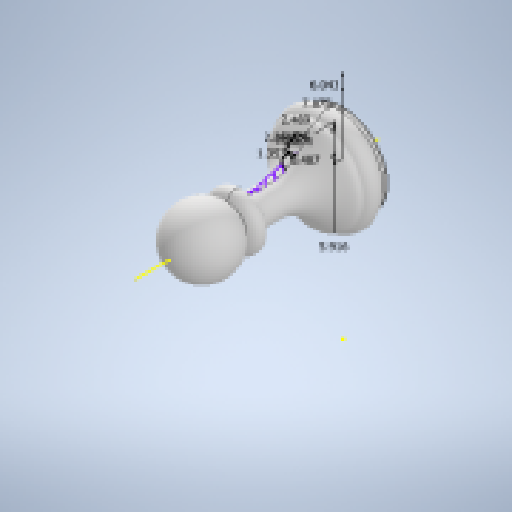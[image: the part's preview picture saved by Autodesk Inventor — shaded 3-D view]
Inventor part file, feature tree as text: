
AUTODESK INVENTOR PART (.ipt)
format: ipt  version: 2024.1 (Build 281209000, 209)  size: 1,490,432 bytes
history: native  units: mm
features: other x13, sketch x10, extrude x7, pattern_circular x3, revolve x1, chamfer x1, plane x1, emboss x1, helix x1, projected_geometry x1
ambient origin geometry x8: Origin, YZ Plane, XZ Plane, XY Plane, X Axis, Y Axis, Z Axis, Center Point
bodies: Solid1 (feature_tree)
feature tree (39):
  extrude  "Extrusion1"  Depth=3.0mm TaperAngle=0.0deg
  other  "Work Axis1"
  extrude  "Extrusion2"  Depth=23.0mm
  revolve  "Revolution1"  [1 undecoded]
  chamfer  "Chamfer1"  Distance=3.0mm
  sketch  "Sketch11"  dims[d37=120.0mm d38=360.0deg d40=10.0mm d41=0.0mm]
  extrude  "Extrusion6"  Depth=2.0mm TaperAngle=0.0deg
  extrude  "Extrusion7"  Depth=0.3mm TaperAngle=0.0deg
  extrude  "Extrusion8"  Depth=10.0mm TaperAngle=0.0deg
  extrude  "Extrusion9"  Depth=0.4mm TaperAngle=0.0deg
  pattern_circular  "Circular Pattern4"  [2 undecoded]
  plane  "Work Plane5"
  sketch  "3D Sketch3"
  emboss  "Emboss1"
  pattern_circular  "Circular Pattern3"  [2 undecoded]
  helix  "Coil1"  [1 undecoded]
  extrude  "Extrusion4"  Depth=5.915933mm
  pattern_circular  "Circular Pattern2"  [2 undecoded]
  sketch  "Sketch1"  dims[d0=10.0mm d1=3.0mm d2=0.0mm]
  sketch  "Sketch2"  dims[d3=10.5mm d4=23.0mm]
  sketch  "Sketch3"  dims[d5=360.0deg d6=14.3mm d7=3.0mm d8=0.0mm]
  projected_geometry  "Projected Loop1"
  sketch  "Sketch5"  dims[d9=0.5mm d10=2.0mm d11=45.0deg d17=2.0mm d18=0.0mm]
  sketch  "Sketch6"  dims[d19=100.0mm d20=360.0deg]
  sketch  "Sketch9"  dims[d22=1.0mm d23=10.0mm d24=50.0mm d25=-0.174533mm d26=90.0deg d27=90.0deg d28=0.0mm d29=0.0mm d35=0.3mm d36=0.0mm]
  other  "Work Axis2"
  other  "Work Axis3"
  other  "Work Axis4"
  other  "Work Axis5"
  other  "Work Axis6"
  other  "Work Axis7"
  other  "Work Axis8"
  other  "Work Axis9"
  other  "Work Axis10"
  other  "Work Axis11"
  other  "Work Axis12"
  other  "Curve On Face1"
  sketch  "Sketch12"  dims[d42=4.15mm d43=0.0mm d44=0.4mm d45=0.0mm]
  sketch  "Sketch13"  dims[d51=6.042539mm d52=2.314913mm d53=2.489147mm d54=7.875064mm d55=5.915933mm d57=0.487336mm d58=0.259822mm d59=1.352868mm d60=2.004443mm d61=0.435462mm d64=10.0mm d65=0.0mm d66=5.0mm d67=0.3mm d68=0.0mm d69=0.0mm d70=60.0mm d71=360.0deg]
note: 8 required parameter values undecoded (feature->parameter linkage not recoverable at this tier; creation-order binding heuristic only, values carry confidence <= 0.55)